# Revit family: Electrical-Box_FSR_WBMS3G
name_source: partatom
category: Electrical Fixtures
units: mm (PartAtom-declared; Revit-internal decimal feet)

## family parameters
Always vertical = Yes
Classification Number = 23.85.10.17.11
Cut with Voids When Loaded = No
Host = Wall
Maintain Annotation Orientation = No
Part Type = Normal
Room Calculation Point = No
Round Connector Dimension = Use Diameter
Shared = No

## types (3) — shared parameters
Alto tapa = -1 1/2"
Assembly Code = D5020100
Body Material = Material and Finish as Specified in 26 27 26
Building Codes = ftp://doclib.fsrinc.com/
Construction Details = ftp://doclib.fsrinc.com/
Default Elevation = 0"
Green Building-LEED = http://www.arcat.com
Gross Depth = 3"
Gross Height = 15 1/2"
Gross Projection = 15"
Gross Width = 14"
Installation-Fabrication = ftp://doclib.fsrinc.com/
Keynote = 26 27 26
Manufacturer = FSR Inc.
Manufacturer Fax = 973-785-4207
Manufacturer Website = http://www.fsrinc.com
Model = WB-MS3G
Product Data = http://www.arcat.com
Sales Information = http://www.fsrinc.com
Specification = http://www.arcat.com
Test Data = ftp://doclib.fsrinc.com/
Trim Material = Material and Finish as Specified in 26 27 26
URL = http://www.fsrinc.com
zero-valued in all types: Expected Lifespan (Years), Maintenance Schedule (Months), Warranty Duration (Years)

## per-type parameters (varying)
| type | Cover Material | Description |
| Finish as Specified | Finish as Specified | FSR WB-MS3G - 3 Gang - Finish as Specified |
| Primed Finish | Prime Paint | FSR WB-MS3G - 3 Gang - Primed Finish |
| White Finish | White | FSR WB-MS3G - 3 Gang - White Finish |

## geometry (parser evidence)
native form markers: Sweep x2
no freeform markers — native parametric forms only
